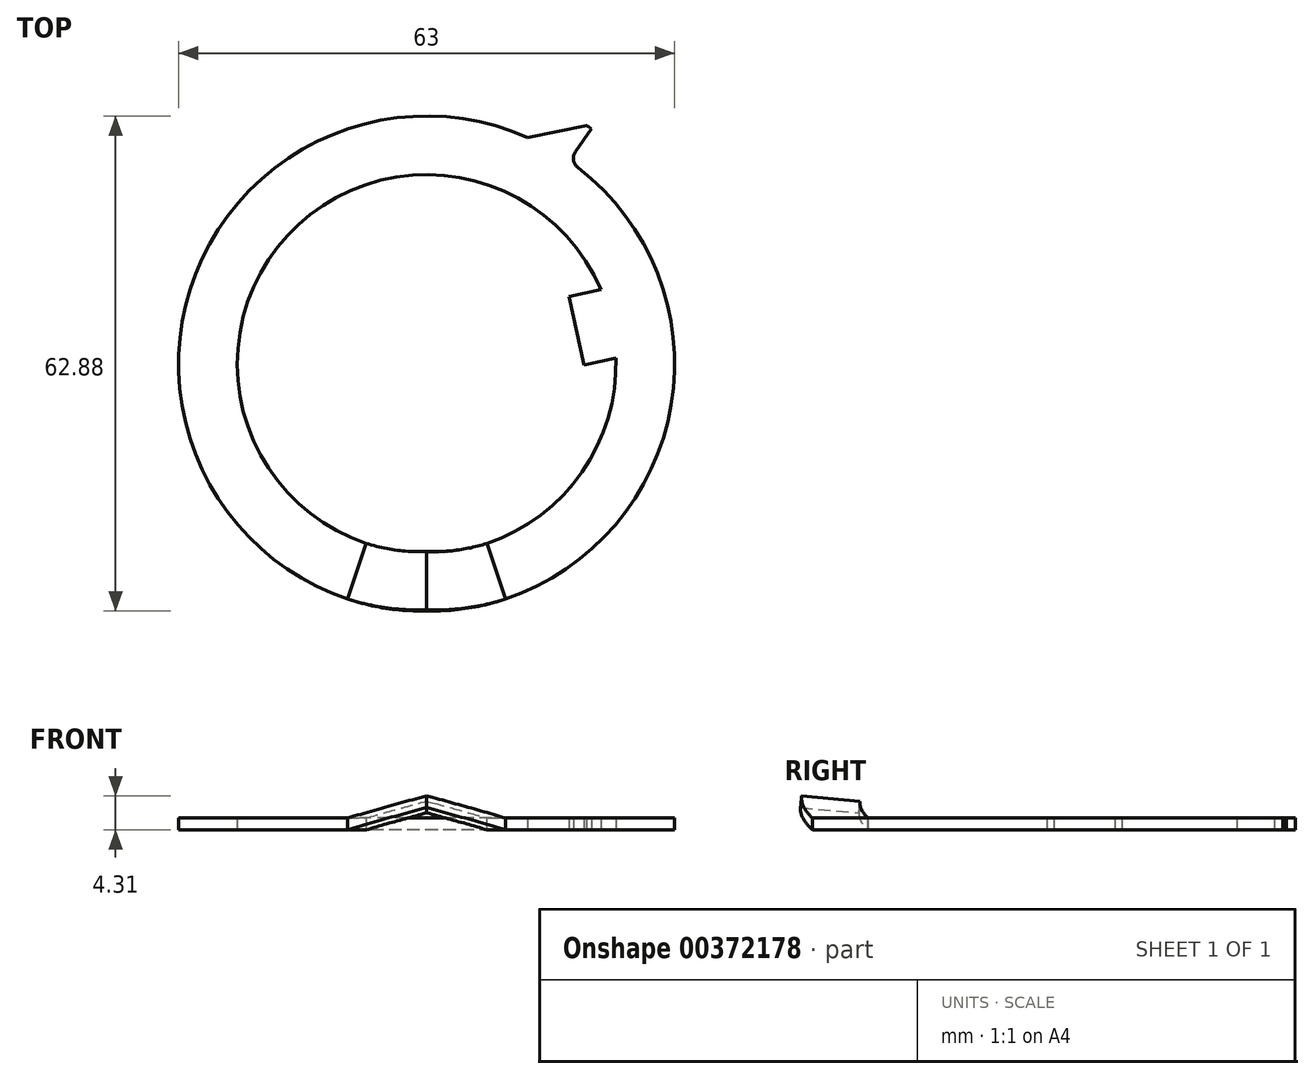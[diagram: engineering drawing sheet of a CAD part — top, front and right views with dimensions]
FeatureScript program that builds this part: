
annotation { "Feature Type Name" : "Feature", "Feature Type Description" : "" }
export const myFeature = defineFeature(function(context is Context, id is Id, definition is map)
    precondition{}
    {
        {
            var Q0;
            Q0=qCreatedBy(makeId("Top.planeOp"),FACE);
            var sketch = newSketch(context, id + "F0", { "sketchPlane" : qUnion([Q0])});
            skArc(sketch, "E0", {"start": v(4.27, 9.6) * mm, "mid": v(-9.78, 3.81) * mm, "end": v(-3.35, -9.95) * mm});
            skArc(sketch, "E1", {"start": v(7.37, 3.15) * mm, "mid": v(-5.89, 5.44) * mm, "end": v(-2.56, -7.6) * mm});
            skLineSegment(sketch, "E2", {"start": v(0, 0) * mm, "end": v(6.35, 1.4) * mm, "construction": true});
            skLineSegment(sketch, "E3", {"start": v(6.67, -0.04) * mm, "end": v(6.03, 2.85) * mm});
            skLineSegment(sketch, "E4", {"start": v(6.67, -0.04) * mm, "end": v(8.01, 0.26) * mm});
            skLineSegment(sketch, "E5", {"start": v(6.03, 2.85) * mm, "end": v(7.37, 3.15) * mm});
            skLineSegment(sketch, "E6", {"start": v(6.3, 9) * mm, "end": v(6.97, 9.96) * mm});
            skArc(sketch, "E7", {"start": v(6.97, 9.96) * mm, "mid": v(6.87, 10.03) * mm, "end": v(6.77, 10.1) * mm});
            skLineSegment(sketch, "E8", {"start": v(6.77, 10.1) * mm, "end": v(4.27, 9.6) * mm});
            skLineSegment(sketch, "E9", {"start": v(4.27, 9.6) * mm, "end": v(0, 0) * mm, "construction": true});
            skLineSegment(sketch, "E10", {"start": v(6.02, 8.6) * mm, "end": v(0, 0) * mm, "construction": true});
            skArc(sketch, "E11", {"start": v(6.3, 9) * mm, "mid": v(6.22, 8.64) * mm, "end": v(6.4, 8.32) * mm});
            skLineSegment(sketch, "E12", {"start": v(3.35, -9.95) * mm, "end": v(2.56, -7.6) * mm});
            skLineSegment(sketch, "E13", {"start": v(-3.35, -9.95) * mm, "end": v(-2.56, -7.6) * mm});
            skArc(sketch, "E14.trimOffspring", {"start": v(2.56, -7.6) * mm, "mid": v(6.59, -4.57) * mm, "end": v(8.01, 0.26) * mm});
            skArc(sketch, "E15.trimOffspring", {"start": v(3.35, -9.95) * mm, "mid": v(10.36, -1.73) * mm, "end": v(6.4, 8.32) * mm});
            skSolve(sketch);
        }
        {
            var Q0;
            Q0=makeQuery(id+"F0.imprint","IMPRINT",FACE,{"disambiguationData":[TD([[makeQuery(id+"F0.imprint","IMPRINT",EDGE,{"derivedFrom":sQuery(id+"F0.wireOp",EDGE,"E0")}),1.0]])]});
            extrude(context, id + "F1", {"entities" : qUnion([Q0]), "depth" : 0.5 * mm});
        }
        {
            var Q0;
            Q0=makeQuery(id+"F1.opExtrude","CAP_EDGE",EDGE,{"disambiguationData":[OSD([sQuery(id+"F0.wireOp",EDGE,"E12")])],"isStart":true});
            cPlane(context, id + "F2", {"entities" : qUnion([Q0]), "cplaneType" : CPlaneType.LINE_ANGLE, "offset" : 150 * mm, "angle" : 15.77 * degree, "width" : 150 * mm, "height" : 150 * mm});
        }
        {
            var Q0;
            Q0=qCreatedBy(id+"F2.planeOp",FACE);
            var sketch = newSketch(context, id + "F3", { "sketchPlane" : qUnion([Q0])});
            skArc(sketch, "E16", {"start": v(0, -8) * mm, "mid": v(1.34, -7.89) * mm, "end": v(2.65, -7.55) * mm});
            skArc(sketch, "E17", {"start": v(0, -10.5) * mm, "mid": v(1.76, -10.35) * mm, "end": v(3.47, -9.91) * mm});
            skLineSegment(sketch, "E18", {"start": v(2.65, -7.55) * mm, "end": v(3.47, -9.91) * mm});
            skLineSegment(sketch, "E19", {"start": v(0, -8) * mm, "end": v(0, -10.5) * mm});
            skSolve(sketch);
        }
        {
            var Q0;
            Q0=makeQuery(id+"F1.opExtrude","CAP_EDGE",EDGE,{"disambiguationData":[OSD([sQuery(id+"F0.wireOp",EDGE,"E13")])],"isStart":true});
            cPlane(context, id + "F4", {"entities" : qUnion([Q0]), "cplaneType" : CPlaneType.LINE_ANGLE, "offset" : 150 * mm, "angle" : 164.23 * degree, "width" : 150 * mm, "height" : 150 * mm});
        }
        {
            var Q0;
            Q0=qCreatedBy(id+"F4.planeOp",FACE);
            var sketch = newSketch(context, id + "F5", { "sketchPlane" : qUnion([Q0])});
            skArc(sketch, "E20", {"start": v(0, 8) * mm, "mid": v(-1.34, 7.89) * mm, "end": v(-2.65, 7.55) * mm});
            skArc(sketch, "E21", {"start": v(0, 10.5) * mm, "mid": v(-1.76, 10.35) * mm, "end": v(-3.47, 9.91) * mm});
            skLineSegment(sketch, "E22", {"start": v(-2.65, 7.55) * mm, "end": v(-3.47, 9.91) * mm});
            skLineSegment(sketch, "E23", {"start": v(0, 8) * mm, "end": v(0, 10.5) * mm});
            skSolve(sketch);
        }
        {
            var Q0;
            Q0=makeQuery(id+"F1.opExtrude","SWEPT_FACE",FACE,{"disambiguationData":[OSD([sQuery(id+"F0.wireOp",EDGE,"E13")])]});
            var Q1;
            Q1=sQuery(id+"F5.wireOp",EDGE,"E21");
            var Q2;
            Q2=sQuery(id+"F3.wireOp",EDGE,"E17");
            sweep(context, id + "F6", {"operationType" : NewBodyOperationType.ADD, "profiles" : qUnion([Q0]), "path" : qUnion([Q1, Q2])});
        }
        {
            var Q0;
            Q0=makeQuery(id+"F1.opExtrude","SWEPT_BODY",BODY,{"disambiguationData":[OSD([sQuery(id+"F0.wireOp",EDGE,"E0"),sQuery(id+"F0.wireOp",EDGE,"E1"),sQuery(id+"F0.wireOp",EDGE,"E3"),sQuery(id+"F0.wireOp",EDGE,"E4"),sQuery(id+"F0.wireOp",EDGE,"E5"),sQuery(id+"F0.wireOp",EDGE,"E6"),sQuery(id+"F0.wireOp",EDGE,"E7"),sQuery(id+"F0.wireOp",EDGE,"E8"),sQuery(id+"F0.wireOp",EDGE,"E11"),sQuery(id+"F0.wireOp",EDGE,"E12"),sQuery(id+"F0.wireOp",EDGE,"E13"),sQuery(id+"F0.wireOp",EDGE,"E14.trimOffspring"),sQuery(id+"F0.wireOp",EDGE,"E15.trimOffspring")])]});
            var Q1;
            Q1=qCreatedBy(makeId("Origin.pointOp"),VERTEX);
            transform(context, id + "F7", {"entities" : qUnion([Q0]), "transformType" : TransformType.SCALE_UNIFORMLY, "scale" : 3, "makeCopy" : false, "scalePoint" : qUnion([Q1])});
        }
    });
